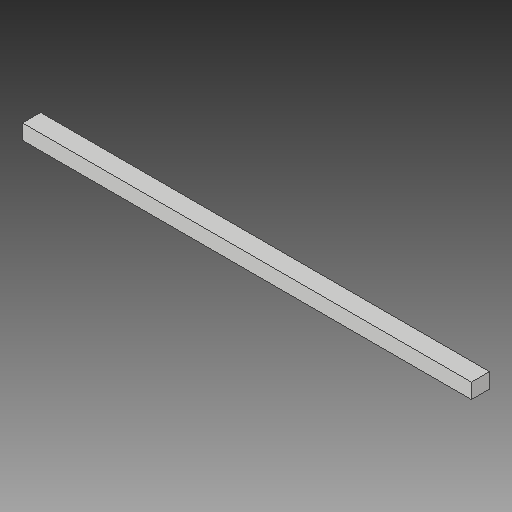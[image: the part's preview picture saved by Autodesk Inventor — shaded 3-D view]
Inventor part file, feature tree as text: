
AUTODESK INVENTOR PART (.ipt)
format: ipt  version: 2019 (Build 230136000, 136)  size: 93,184 bytes
history: native  units: mm
features: extrude x1, sketch x1
ambient origin geometry x8: Origin, YZ Plane, XZ Plane, XY Plane, X Axis, Y Axis, Z Axis, Center Point
bodies: Solid1 (feature_tree)
feature tree (2):
  extrude  "Extrusion1"  Depth=5.0mm
  sketch  "Sketch1"  dims[d0=148.627mm d1=5.0mm d2=6.0mm d3=0.0mm]
